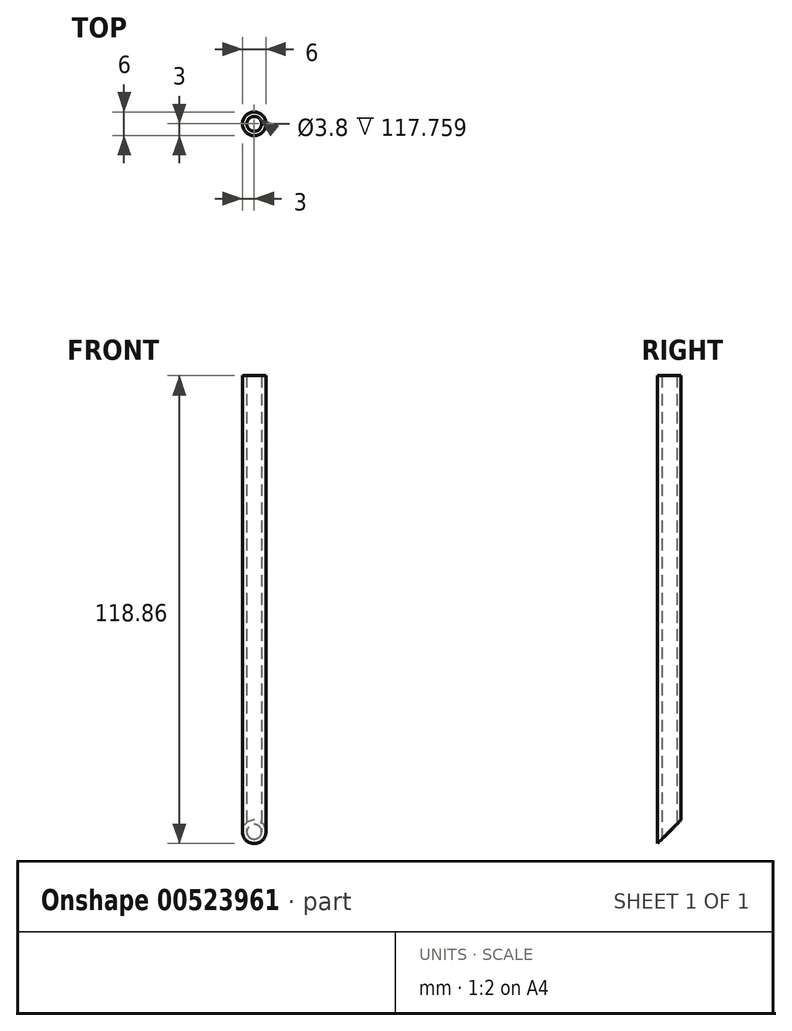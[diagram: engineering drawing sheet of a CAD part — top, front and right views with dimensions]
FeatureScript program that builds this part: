
annotation { "Feature Type Name" : "Feature", "Feature Type Description" : "" }
export const myFeature = defineFeature(function(context is Context, id is Id, definition is map)
    precondition{}
    {
        {
            var Q0;
            Q0=qCreatedBy(makeId("Top.planeOp"),FACE);
            var sketch = newSketch(context, id + "F0", { "sketchPlane" : qUnion([Q0])});
            skCircle(sketch, "E0", {"center": v(0, 0) * mm, "radius": 3 * mm});
            skSolve(sketch);
        }
        {
            var Q0;
            Q0=makeQuery(id+"F0.imprint","IMPRINT",FACE,{"disambiguationData":[TD([[makeQuery(id+"F0.imprint","IMPRINT",EDGE,{"derivedFrom":sQuery(id+"F0.wireOp",EDGE,"E0")}),1.0]])]});
            extrude(context, id + "F1", {"entities" : qUnion([Q0]), "depth" : 130 * mm, "offsetDistance" : 25 * mm});
        }
        {
            var Q0;
            Q0=makeQuery(id+"F1.opExtrude","CAP_FACE",FACE,{"disambiguationData":[OSD([sQuery(id+"F0.wireOp",EDGE,"E0")])],"isStart":false});
            shell(context, id + "F2", {"entities" : qUnion([Q0]), "thickness" : 1.1 * mm});
        }
        {
            var Q0;
            Q0=qCreatedBy(makeId("Front.planeOp"),FACE);
            var Q1;
            Q1=qCreatedBy(makeId("Top.planeOp"),FACE);
            cPlane(context, id + "F3", {"entities" : qUnion([Q0, Q1]), "cplaneType" : CPlaneType.MID_PLANE, "offset" : 25 * mm, "flipAlignment" : true, "width" : 150 * mm, "height" : 150 * mm});
        }
        {
            var Q0;
            Q0=qCreatedBy(id+"F3.planeOp",FACE);
            cPlane(context, id + "F4", {"entities" : qUnion([Q0]), "cplaneType" : CPlaneType.OFFSET, "offset" : 10 * mm, "width" : 150 * mm, "height" : 150 * mm});
        }
        {
            var Q0;
            Q0=qCreatedBy(id+"F4.planeOp",FACE);
            var sketch = newSketch(context, id + "F5", { "sketchPlane" : qUnion([Q0])});
            skCircle(sketch, "E1", {"center": v(0, 0) * mm, "radius": 26.26 * mm});
            skSolve(sketch);
        }
        {
            var Q0;
            Q0 = qSketchRegion(id + "F5", true);
            extrude(context, id + "F6", {"entities" : qUnion([Q0]), "operationType" : NewBodyOperationType.REMOVE, "oppositeDirection" : true, "depth" : 25 * mm, "offsetDistance" : 25 * mm});
        }
    });
